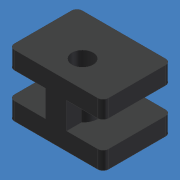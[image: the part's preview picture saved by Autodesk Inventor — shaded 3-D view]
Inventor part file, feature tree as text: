
AUTODESK INVENTOR PART (.ipt)
format: ipt  version: 2012 (Build 160160000, 160)  size: 131,072 bytes
history: native  units: mm (DEFAULTED — no unit token found)
features: sketch x4, extrude x3, fillet x1, plane x1, other x1, revolve x1
ambient origin geometry x8: Origin, YZ Plane, XZ Plane, XY Plane, X Axis, Y Axis, Z Axis, Center Point
bodies: Solid1 (feature_tree)
feature tree (11):
  extrude  "Extrusion1"  Depth=6.4mm
  fillet  "Fillet1"  Radius=5.82mm
  extrude  "Extrusion2"  Depth=3.9mm
  plane  "Work Plane1"
  other  "Work Axis1"
  revolve  "Revolution1"  [1 undecoded]
  extrude  "Extrusion3"  Depth=1.5mm
  sketch  "Sketch1"  dims[d0=8.87mm d1=6.4mm d2=5.82mm d3=0.0mm]
  sketch  "Sketch2"  dims[d4=0.5mm d5=3.9mm]
  sketch  "Sketch5"  dims[d6=2.0mm d7=5.82mm d8=0.0mm]
  sketch  "Sketch6"  dims[d9=-3.9mm d10=1.5mm d11=1.66mm d12=1.66mm d13=90.0deg d14=5.82mm d15=0.0mm]
note: 1 required parameter value undecoded (feature->parameter linkage not recoverable at this tier; creation-order binding heuristic only, values carry confidence <= 0.55)
